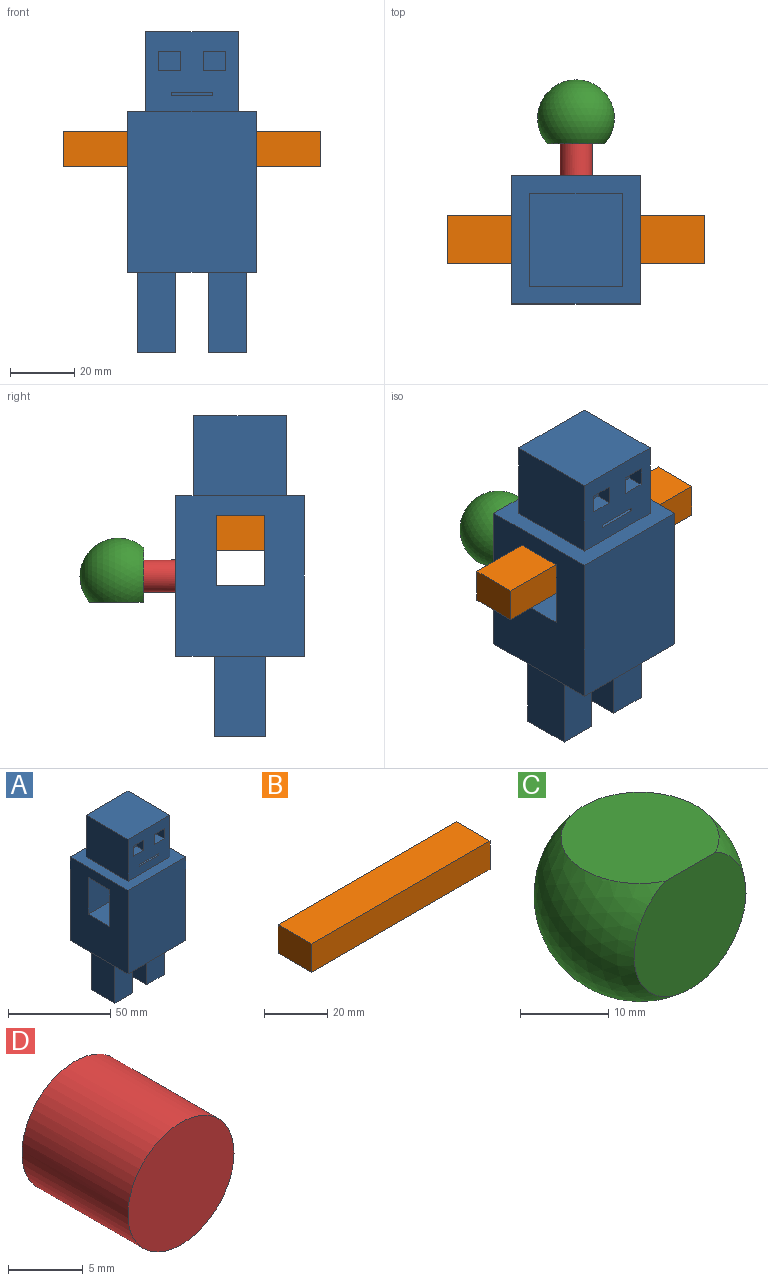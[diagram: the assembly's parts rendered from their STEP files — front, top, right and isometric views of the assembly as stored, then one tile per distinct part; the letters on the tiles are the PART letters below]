
ASSEMBLY  parts=4 mates=3
PART A: 42 faces, bbox 40x40x100 mm
  f0: plane 29x25mm, normal (0,-1,0), area 628mm2, adj f6,f21,f23,f24,f27,f28,f29,f30
  f1: plane 40x40mm, normal (0,0,-1), area 1216mm2, adj f2,f3,f4,f5,f11,f12,f13,f14
  f2: plane 50x40mm, normal (0,-1,0), area 2000mm2, adj f1,f3,f5,f6
  f3: plane 50x40mm, normal (1,0,0), area 1670mm2, adj f1,f2,f4,f6,f7,f8,f9,f10
  f4: plane 50x40mm, normal (0,1,0), area 1921.5mm2, adj f1,f3,f5,f6,f25
  f5: plane 50x40mm, normal (-1,0,0), area 1670mm2, adj f1,f2,f4,f6,f7,f8,f9,f10
  f6: plane 40x40mm, normal (0,0,1), area 759mm2, adj f0,f2,f3,f4,f5,f21,f22,f23
  f7: plane 40x22mm, normal (0,1,0), area 880mm2, adj f3,f5,f8,f10
  f8: plane 40x15mm, normal (0,0,1), area 600mm2, adj f3,f5,f7,f9
  f9: plane 40x22mm, normal (0,-1,0), area 880mm2, adj f3,f5,f8,f10
  f10: plane 40x15mm, normal (0,0,-1), area 600mm2, adj f3,f5,f7,f9
  f11: plane 25x16mm, normal (1,0,0), area 400mm2, adj f1,f12,f14,f15
  f12: plane 25x12mm, normal (0,-1,0), area 300mm2, adj f1,f11,f13,f15
  f13: plane 25x16mm, normal (-1,0,0), area 400mm2, adj f1,f12,f14,f15
  f14: plane 25x12mm, normal (0,1,0), area 300mm2, adj f1,f11,f13,f15
  f15: plane 16x12mm, normal (0,0,-1), area 192mm2, adj f11,f12,f13,f14
  f16: plane 25x16mm, normal (-1,0,0), area 400mm2, adj f1,f17,f19,f20
  f17: plane 25x12mm, normal (0,1,0), area 300mm2, adj f1,f16,f18,f20
  f18: plane 25x16mm, normal (1,0,0), area 400mm2, adj f1,f17,f19,f20
  f19: plane 25x12mm, normal (0,-1,0), area 300mm2, adj f1,f16,f18,f20
  f20: plane 16x12mm, normal (0,0,-1), area 192mm2, adj f16,f17,f18,f19
  f21: plane 29x25mm, normal (1,0,0), area 725mm2, adj f0,f6,f22,f24
  f22: plane 29x25mm, normal (0,1,0), area 725mm2, adj f6,f21,f23,f24
  f23: plane 29x25mm, normal (-1,0,0), area 725mm2, adj f0,f6,f22,f24
  f24: plane 29x29mm, normal (0,0,1), area 841mm2, adj f0,f21,f22,f23
  f25: cylinder r=5mm len=10mm, axis (0,1,0), area 314.2mm2, adj f4,f26
  f26: plane 10x10mm, normal (0,1,0), area 78.5mm2, adj f25
  f27: plane 6x5mm, normal (1,0,0), area 30mm2, adj f0,f28,f30,f31
  f28: plane 7x5mm, normal (0,0,1), area 35mm2, adj f0,f27,f29,f31
  f29: plane 6x5mm, normal (-1,0,0), area 30mm2, adj f0,f28,f30,f31
  f30: plane 7x5mm, normal (0,0,-1), area 35mm2, adj f0,f27,f29,f31
  f31: plane 7x6mm, normal (0,-1,0), area 42mm2, adj f27,f28,f29,f30
  f32: plane 6x5mm, normal (-1,0,0), area 30mm2, adj f0,f33,f35,f36
  f33: plane 7x5mm, normal (0,0,-1), area 35mm2, adj f0,f32,f34,f36
  f34: plane 6x5mm, normal (1,0,0), area 30mm2, adj f0,f33,f35,f36
  f35: plane 7x5mm, normal (0,0,1), area 35mm2, adj f0,f32,f34,f36
  f36: plane 7x6mm, normal (0,-1,0), area 42mm2, adj f32,f33,f34,f35
  f37: plane 5x1mm, normal (1,0,0), area 5mm2, adj f0,f38,f40,f41
  f38: plane 13x5mm, normal (0,0,1), area 65mm2, adj f0,f37,f39,f41
  f39: plane 5x1mm, normal (-1,0,0), area 5mm2, adj f0,f38,f40,f41
  f40: plane 13x5mm, normal (0,0,-1), area 65mm2, adj f0,f37,f39,f41
  f41: plane 13x1mm, normal (0,-1,0), area 13mm2, adj f37,f38,f39,f40
PART B: 6 faces, bbox 80x15x11 mm
  f0: plane 80x11mm, normal (0,1,0), area 880mm2, adj f1,f3,f4,f5
  f1: plane 80x15mm, normal (0,0,1), area 1200mm2, adj f0,f2,f4,f5
  f2: plane 80x11mm, normal (0,-1,0), area 880mm2, adj f1,f3,f4,f5
  f3: plane 80x15mm, normal (0,0,-1), area 1200mm2, adj f0,f2,f4,f5
  f4: plane 15x11mm, normal (-1,0,0), area 165mm2, adj f0,f1,f2,f3
  f5: plane 15x11mm, normal (1,0,0), area 165mm2, adj f0,f1,f2,f3
PART C: 3 faces, bbox 24x20x24 mm
  f0: sphere r=12mm, area 1213.7mm2, adj f1,f2
  f1: plane 17.89x16.94mm, normal (0,-1,0), area 246.2mm2, adj f0,f2
  f2: plane 17.89x16.94mm, normal (0,0,1), area 246.2mm2, adj f0,f1
PART D: 3 faces, bbox 10x10x10 mm
  f0: plane 10x10mm, normal (0,-1,0), area 78.5mm2, adj f1
  f1: cylinder r=5mm len=10mm, axis (0,1,0), area 314.2mm2, adj f0,f2
  f2: plane 10x10mm, normal (0,1,0), area 78.5mm2, adj f1
PLACE A at identity
PLACE B at identity
PLACE C rot(axis=(0,-1,0),180deg) t=(0,0,-0.17)mm
PLACE D at identity
MATE revolute C.f1 <-> D.f1  axis (0,-1,0) through (0,30,0)mm
MATE cylindrical D.f1 <-> A.f25  axis (0,-1,0) through (0,20,0)mm
MATE slider B.f1 <-> A.f10  axis (0,0,1) through (0,0,19)mm
